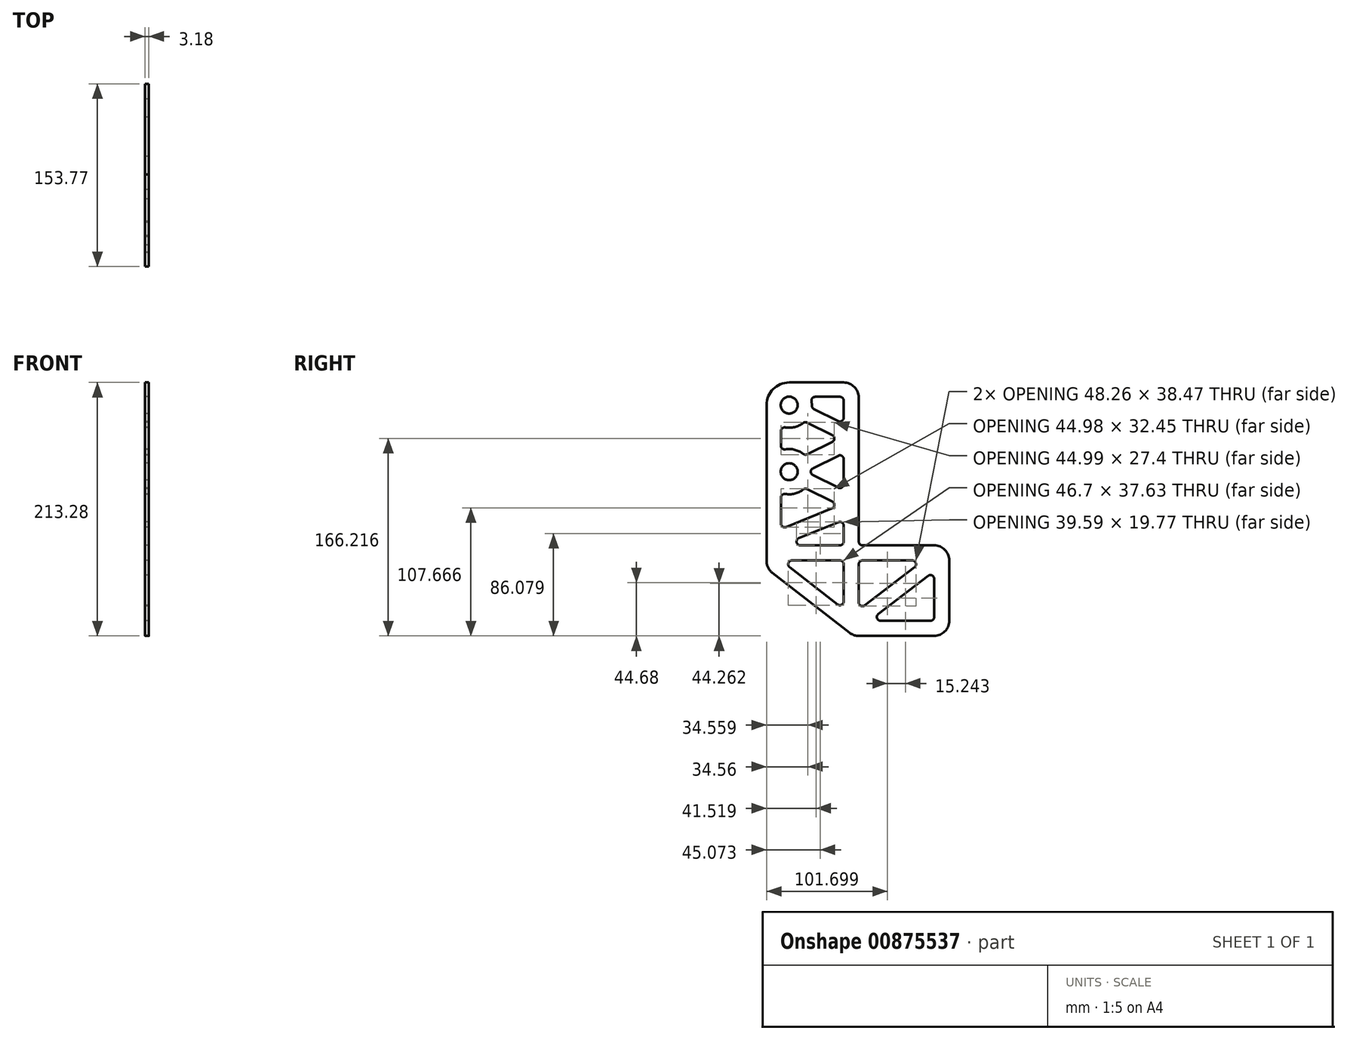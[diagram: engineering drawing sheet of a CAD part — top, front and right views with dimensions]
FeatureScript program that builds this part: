
annotation { "Feature Type Name" : "Feature", "Feature Type Description" : "" }
export const myFeature = defineFeature(function(context is Context, id is Id, definition is map)
    precondition{}
    {
        {
            var Q0;
            Q0=qCreatedBy(makeId("Right.planeOp"),FACE);
            var sketch = newSketch(context, id + "F0", { "sketchPlane" : qUnion([Q0])});
            skLineSegment(sketch, "E0.bottom", {"start": v(25.4, -41.28) * mm, "end": v(-34.93, -41.28) * mm});
            skLineSegment(sketch, "E0.top", {"start": v(38.1, 41.28) * mm, "end": v(-38.1, 41.27) * mm, "construction": true});
            skLineSegment(sketch, "E0.left", {"start": v(38.1, -41.27) * mm, "end": v(38.1, 41.28) * mm, "construction": true});
            skLineSegment(sketch, "E0.right", {"start": v(-38.1, -38.1) * mm, "end": v(-38.1, 41.27) * mm});
            skPoint(sketch, "E0.middle", {"position": v(0, 0) * mm});
            skCircle(sketch, "E1", {"center": v(0, 28.58) * mm, "radius": 6.35 * mm, "construction": true});
            skLineSegment(sketch, "E2", {"start": v(0, 28.57) * mm, "end": v(-38.1, 47.58) * mm, "construction": true});
            skLineSegment(sketch, "E3", {"start": v(0, 28.57) * mm, "end": v(-38.1, 25.48) * mm, "construction": true});
            skLineSegment(sketch, "E4", {"start": v(0, 28.58) * mm, "end": v(-38.1, 28.57) * mm, "construction": true});
            skLineSegment(sketch, "E5", {"start": v(38.1, -53.98) * mm, "end": v(38.1, -104.78) * mm});
            skLineSegment(sketch, "E6", {"start": v(-38.1, 47.58) * mm, "end": v(-795.56, 425.31) * mm, "construction": true});
            skLineSegment(sketch, "E7", {"start": v(-795.56, 425.31) * mm, "end": v(-1159.25, 606.68) * mm, "construction": true});
            skLineSegment(sketch, "E8", {"start": v(-1159.25, 606.68) * mm, "end": v(-1295.27, 333.92) * mm, "construction": true});
            skLineSegment(sketch, "E9", {"start": v(38.1, -117.48) * mm, "end": v(38.1, -1990.73) * mm, "construction": true});
            skLineSegment(sketch, "E10", {"start": v(-1295.27, 333.92) * mm, "end": v(-1295.27, -1990.73) * mm, "construction": true});
            skLineSegment(sketch, "E11", {"start": v(-1295.27, -1990.73) * mm, "end": v(38.1, -1990.73) * mm, "construction": true});
            skLineSegment(sketch, "E12", {"start": v(-860.82, -41.27) * mm, "end": v(-1265.64, -77.12) * mm, "construction": true});
            skLineSegment(sketch, "E13", {"start": v(-1265.64, -77.12) * mm, "end": v(-1238.76, -380.73) * mm, "construction": true});
            skLineSegment(sketch, "E14", {"start": v(-1238.76, -380.73) * mm, "end": v(-1238.76, -1990.73) * mm, "construction": true});
            skCircle(sketch, "E15", {"center": v(-96.62, 76.76) * mm, "radius": 6.99 * mm});
            skCircle(sketch, "E16", {"center": v(-96.62, 20.74) * mm, "radius": 6.99 * mm});
            skLineSegment(sketch, "E17", {"start": v(-860.82, -41.28) * mm, "end": v(-89.66, 21.3) * mm, "construction": true});
            skLineSegment(sketch, "E18", {"start": v(-38.1, 47.58) * mm, "end": v(-38.1, 83.1) * mm});
            skLineSegment(sketch, "E19", {"start": v(-38.1, 47.58) * mm, "end": v(-38.1, 41.28) * mm});
            skArc(sketch, "E20", {"start": v(-99.88, 57.99) * mm, "mid": v(-91.97, 58.28) * mm, "end": v(-84.86, 61.77) * mm});
            skLineSegment(sketch, "E21", {"start": v(-115.67, 76.76) * mm, "end": v(-115.67, 19.19) * mm});
            skLineSegment(sketch, "E22", {"start": v(-115.67, 19.19) * mm, "end": v(-115.67, -54.47) * mm});
            skLineSegment(sketch, "E23", {"start": v(-110.75, -64.5) * mm, "end": v(-45.88, -114.81) * mm});
            skLineSegment(sketch, "E24", {"start": v(-103.6, -1.16) * mm, "end": v(-103.6, -22.87) * mm});
            skLineSegment(sketch, "E25", {"start": v(25.4, -117.48) * mm, "end": v(-38.1, -117.48) * mm});
            skLineSegment(sketch, "E26", {"start": v(-81.48, 35.38) * mm, "end": v(-60.37, 45.9) * mm});
            skLineSegment(sketch, "E27", {"start": v(-81.48, 62.11) * mm, "end": v(-60.37, 51.59) * mm});
            skLineSegment(sketch, "E28", {"start": v(-75.81, 73.48) * mm, "end": v(-55.4, 63.3) * mm});
            skLineSegment(sketch, "E29", {"start": v(-103.6, 76.76) * mm, "end": v(-103.6, 76.76) * mm});
            skLineSegment(sketch, "E30", {"start": v(-96.62, 95.8) * mm, "end": v(-50.8, 95.8) * mm});
            skLineSegment(sketch, "E31", {"start": v(-74.72, 83.74) * mm, "end": v(-53.98, 83.74) * mm});
            skPoint(sketch, "E32", {"position": v(-83.38, 34.43) * mm});
            skPoint(sketch, "E33", {"position": v(-50.8, 46.81) * mm});
            skPoint(sketch, "E34", {"position": v(-83.38, 63.06) * mm});
            skPoint(sketch, "E35", {"position": v(-77.71, 74.42) * mm});
            skPoint(sketch, "E36", {"position": v(-50.8, 83.74) * mm});
            skPoint(sketch, "E37", {"position": v(-83.38, 7.04) * mm});
            skLineSegment(sketch, "E38", {"start": v(-55.92, -90.95) * mm, "end": v(-96.27, -59.66) * mm});
            skLineSegment(sketch, "E39", {"start": v(-94.33, -53.98) * mm, "end": v(-53.97, -53.98) * mm});
            skLineSegment(sketch, "E40", {"start": v(-60.6, -10.22) * mm, "end": v(-99.24, -25.82) * mm});
            skLineSegment(sketch, "E41", {"start": v(-55.16, -21.72) * mm, "end": v(-88.45, -35.16) * mm});
            skLineSegment(sketch, "E42", {"start": v(-87.26, -41.28) * mm, "end": v(-53.97, -41.28) * mm});
            skLineSegment(sketch, "E43", {"start": v(-34.92, -53.98) * mm, "end": v(6.98, -53.98) * mm});
            skLineSegment(sketch, "E44", {"start": v(8.91, -59.67) * mm, "end": v(-33, -91.8) * mm});
            skLineSegment(sketch, "E45", {"start": v(-19.68, -104.78) * mm, "end": v(22.23, -104.78) * mm});
            skLineSegment(sketch, "E46", {"start": v(25.4, -101.6) * mm, "end": v(25.4, -69.47) * mm});
            skLineSegment(sketch, "E47", {"start": v(20.3, -66.95) * mm, "end": v(-21.61, -99.08) * mm});
            skArc(sketch, "E48.trimOffspring", {"start": v(-99.88, 1.97) * mm, "mid": v(-91.97, 2.26) * mm, "end": v(-84.86, 5.75) * mm});
            skLineSegment(sketch, "E49.trimOffspring", {"start": v(-50.8, 24.45) * mm, "end": v(-38.1, 25.48) * mm, "construction": true});
            skLineSegment(sketch, "E50.trimOffspring", {"start": v(-103.6, 54.86) * mm, "end": v(-103.6, 42.63) * mm});
            skArc(sketch, "E51.trimOffspring", {"start": v(-96.62, 95.8) * mm, "mid": v(-110.09, 90.23) * mm, "end": v(-115.67, 76.76) * mm});
            skLineSegment(sketch, "E52.trimOffspring", {"start": v(-50.8, 80.57) * mm, "end": v(-50.8, 66.14) * mm});
            skArc(sketch, "E53.trimOffspring", {"start": v(-84.86, 35.72) * mm, "mid": v(-91.97, 39.2) * mm, "end": v(-99.88, 39.5) * mm});
            skLineSegment(sketch, "E54.trimOffspring", {"start": v(-50.8, -57.15) * mm, "end": v(-50.8, -88.45) * mm});
            skLineSegment(sketch, "E55", {"start": v(-50.8, -24.66) * mm, "end": v(-50.8, -38.1) * mm});
            skArc(sketch, "E56.filletArc", {"start": v(-38.1, 83.1) * mm, "mid": v(-41.82, 92.09) * mm, "end": v(-50.8, 95.8) * mm});
            skPoint(sketch, "E57.visualSharp", {"position": v(38.1, -41.28) * mm});
            skArc(sketch, "E57.filletArc", {"start": v(38.1, -53.98) * mm, "mid": v(34.38, -45) * mm, "end": v(25.4, -41.28) * mm});
            skPoint(sketch, "E58.visualSharp", {"position": v(38.1, -117.48) * mm});
            skArc(sketch, "E58.filletArc", {"start": v(25.4, -117.48) * mm, "mid": v(34.38, -113.76) * mm, "end": v(38.1, -104.78) * mm});
            skPoint(sketch, "E59.visualSharp", {"position": v(-115.67, -60.69) * mm});
            skArc(sketch, "E59.filletArc", {"start": v(-115.67, -54.47) * mm, "mid": v(-114.37, -60.06) * mm, "end": v(-110.75, -64.5) * mm});
            skPoint(sketch, "E60.newPointA", {"position": v(-42.45, -117.48) * mm});
            skArc(sketch, "E60.filletArc", {"start": v(-45.88, -114.81) * mm, "mid": v(-42.21, -116.8) * mm, "end": v(-38.1, -117.48) * mm});
            skPoint(sketch, "E61.visualSharp", {"position": v(-50.8, -41.28) * mm});
            skArc(sketch, "E61.filletArc", {"start": v(-53.97, -41.28) * mm, "mid": v(-51.73, -40.35) * mm, "end": v(-50.8, -38.1) * mm});
            skPoint(sketch, "E62.visualSharp", {"position": v(-50.8, -19.96) * mm});
            skArc(sketch, "E62.filletArc", {"start": v(-50.8, -24.66) * mm, "mid": v(-52.2, -22.03) * mm, "end": v(-55.16, -21.72) * mm});
            skPoint(sketch, "E63.visualSharp", {"position": v(-103.6, -41.28) * mm});
            skArc(sketch, "E63.filletArc", {"start": v(-88.45, -35.16) * mm, "mid": v(-90.37, -38.7) * mm, "end": v(-87.26, -41.28) * mm});
            skPoint(sketch, "E64.visualSharp", {"position": v(-103.6, -53.98) * mm});
            skArc(sketch, "E64.filletArc", {"start": v(-94.33, -53.98) * mm, "mid": v(-97.33, -56.12) * mm, "end": v(-96.27, -59.66) * mm});
            skPoint(sketch, "E65.visualSharp", {"position": v(-50.8, -53.98) * mm});
            skArc(sketch, "E65.filletArc", {"start": v(-50.8, -57.15) * mm, "mid": v(-51.73, -54.9) * mm, "end": v(-53.97, -53.98) * mm});
            skPoint(sketch, "E66.visualSharp", {"position": v(-50.8, -94.93) * mm});
            skArc(sketch, "E66.filletArc", {"start": v(-55.92, -90.95) * mm, "mid": v(-52.58, -91.3) * mm, "end": v(-50.8, -88.45) * mm});
            skPoint(sketch, "E67.visualSharp", {"position": v(-38.1, -95.72) * mm});
            skArc(sketch, "E67.filletArc", {"start": v(-38.1, -89.28) * mm, "mid": v(-36.33, -92.13) * mm, "end": v(-33, -91.8) * mm});
            skPoint(sketch, "E68.visualSharp", {"position": v(-38.1, -53.98) * mm});
            skArc(sketch, "E68.filletArc", {"start": v(-34.92, -53.98) * mm, "mid": v(-37.17, -54.9) * mm, "end": v(-38.1, -57.15) * mm});
            skPoint(sketch, "E69.visualSharp", {"position": v(16.34, -53.98) * mm});
            skArc(sketch, "E69.filletArc", {"start": v(8.91, -59.67) * mm, "mid": v(9.99, -56.13) * mm, "end": v(6.98, -53.98) * mm});
            skPoint(sketch, "E70.visualSharp", {"position": v(25.4, -63.03) * mm});
            skArc(sketch, "E70.filletArc", {"start": v(25.4, -69.47) * mm, "mid": v(23.63, -66.62) * mm, "end": v(20.3, -66.95) * mm});
            skPoint(sketch, "E71.visualSharp", {"position": v(-29.04, -104.78) * mm});
            skArc(sketch, "E71.filletArc", {"start": v(-21.61, -99.08) * mm, "mid": v(-22.69, -102.62) * mm, "end": v(-19.68, -104.78) * mm});
            skArc(sketch, "E72.filletArc", {"start": v(22.23, -104.78) * mm, "mid": v(24.47, -103.85) * mm, "end": v(25.4, -101.6) * mm});
            skPoint(sketch, "E73.visualSharp", {"position": v(-103.6, -27.58) * mm});
            skArc(sketch, "E73.filletArc", {"start": v(-103.6, -22.87) * mm, "mid": v(-102.2, -25.5) * mm, "end": v(-99.24, -25.82) * mm});
            skPoint(sketch, "E74.visualSharp", {"position": v(-50.8, -6.26) * mm});
            skArc(sketch, "E74.filletArc", {"start": v(-60.6, -10.22) * mm, "mid": v(-58.62, -7.4) * mm, "end": v(-60.37, -4.43) * mm});
            skPoint(sketch, "E75.visualSharp", {"position": v(-103.6, 3.01) * mm});
            skArc(sketch, "E75.filletArc", {"start": v(-99.88, 1.97) * mm, "mid": v(-102.47, 1.27) * mm, "end": v(-103.6, -1.16) * mm});
            skPoint(sketch, "E76.visualSharp", {"position": v(-38.1, -41.28) * mm});
            skArc(sketch, "E76.filletArc", {"start": v(-38.1, -38.1) * mm, "mid": v(-37.17, -40.35) * mm, "end": v(-34.93, -41.28) * mm});
            skArc(sketch, "E77.filletArc", {"start": v(-84.86, 35.72) * mm, "mid": v(-83.22, 35.06) * mm, "end": v(-81.48, 35.38) * mm});
            skPoint(sketch, "E78.visualSharp", {"position": v(-103.6, 38.46) * mm});
            skArc(sketch, "E78.filletArc", {"start": v(-103.6, 42.63) * mm, "mid": v(-102.47, 40.2) * mm, "end": v(-99.88, 39.5) * mm});
            skPoint(sketch, "E79.visualSharp", {"position": v(-103.6, 59.03) * mm});
            skArc(sketch, "E79.filletArc", {"start": v(-99.88, 57.99) * mm, "mid": v(-102.47, 57.3) * mm, "end": v(-103.6, 54.86) * mm});
            skArc(sketch, "E80.filletArc", {"start": v(-60.37, 45.9) * mm, "mid": v(-58.62, 48.75) * mm, "end": v(-60.37, 51.59) * mm});
            skPoint(sketch, "E81.visualSharp", {"position": v(-78.9, 83.74) * mm});
            skArc(sketch, "E81.filletArc", {"start": v(-74.72, 83.74) * mm, "mid": v(-77.15, 82.61) * mm, "end": v(-77.85, 80.02) * mm});
            skArc(sketch, "E82.filletArc", {"start": v(-50.8, 80.57) * mm, "mid": v(-51.73, 82.81) * mm, "end": v(-53.98, 83.74) * mm});
            skPoint(sketch, "E83.visualSharp", {"position": v(-50.8, 4.98) * mm});
            skLineSegment(sketch, "E84", {"start": v(-50.8, 80.57) * mm, "end": v(-50.8, 61) * mm, "construction": true});
            skArc(sketch, "E85.filletArc", {"start": v(-55.4, 63.3) * mm, "mid": v(-52.3, 63.44) * mm, "end": v(-50.8, 66.14) * mm});
            skLineSegment(sketch, "E86", {"start": v(-38.1, -57.15) * mm, "end": v(-38.1, -89.28) * mm});
            skLineSegment(sketch, "E87", {"start": v(-50.8, 24.45) * mm, "end": v(-96.62, 20.74) * mm, "construction": true});
            skCircle(sketch, "E88", {"center": v(-96.62, 20.74) * mm, "radius": 19.05 * mm, "construction": true});
            skLineSegment(sketch, "E89", {"start": v(-50.8, 61) * mm, "end": v(-55.4, 63.3) * mm, "construction": true});
            skLineSegment(sketch, "E90", {"start": v(-77.71, 74.42) * mm, "end": v(-93.28, 82.9) * mm, "construction": true});
            skLineSegment(sketch, "E91", {"start": v(-50.8, 10.11) * mm, "end": v(-50.8, 31.36) * mm});
            skLineSegment(sketch, "E92", {"start": v(-50.8, 4.98) * mm, "end": v(-50.8, -94.93) * mm, "construction": true});
            skLineSegment(sketch, "E93", {"start": v(-103.6, -22.87) * mm, "end": v(-103.6, -53.98) * mm, "construction": true});
            skArc(sketch, "E94.filletArc", {"start": v(-50.8, 31.36) * mm, "mid": v(-52.3, 34.06) * mm, "end": v(-55.4, 34.2) * mm});
            skLineSegment(sketch, "E95", {"start": v(-50.8, 31.36) * mm, "end": v(-50.8, 46.81) * mm, "construction": true});
            skArc(sketch, "E96.filletArc", {"start": v(-55.4, 7.27) * mm, "mid": v(-52.3, 7.41) * mm, "end": v(-50.8, 10.11) * mm});
            skLineSegment(sketch, "E97", {"start": v(-50.8, 4.98) * mm, "end": v(-50.8, 10.11) * mm, "construction": true});
            skLineSegment(sketch, "E98", {"start": v(-60.6, -10.22) * mm, "end": v(-50.8, -6.26) * mm, "construction": true});
            skLineSegment(sketch, "E99", {"start": v(-53.97, -41.28) * mm, "end": v(-50.8, -41.28) * mm, "construction": true});
            skLineSegment(sketch, "E100", {"start": v(-55.16, -21.72) * mm, "end": v(-50.8, -19.96) * mm, "construction": true});
            skLineSegment(sketch, "E101", {"start": v(-50.8, -94.93) * mm, "end": v(-55.92, -90.95) * mm, "construction": true});
            skLineSegment(sketch, "E102", {"start": v(-67.24, 42.48) * mm, "end": v(-61.57, 31.12) * mm, "construction": true});
            skPoint(sketch, "E103", {"position": v(-64.4, 36.8) * mm});
            skLineSegment(sketch, "E104", {"start": v(-96.62, 20.74) * mm, "end": v(-64.4, 36.8) * mm, "construction": true});
            skLineSegment(sketch, "E105", {"start": v(-67.24, 42.48) * mm, "end": v(-81.48, 35.38) * mm});
            skLineSegment(sketch, "E106", {"start": v(-50.8, 36.49) * mm, "end": v(-55.4, 34.2) * mm, "construction": true});
            skLineSegment(sketch, "E107", {"start": v(-55.4, 34.2) * mm, "end": v(-61.57, 31.12) * mm});
            skLineSegment(sketch, "E108", {"start": v(-67.24, 42.48) * mm, "end": v(-96.85, 27.72) * mm});
            skLineSegment(sketch, "E109", {"start": v(-60.37, -4.43) * mm, "end": v(-81.48, 6.1) * mm});
            skLineSegment(sketch, "E110", {"start": v(-83.38, 7.04) * mm, "end": v(-96.85, 13.75) * mm});
            skLineSegment(sketch, "E111", {"start": v(-50.8, 4.98) * mm, "end": v(-55.4, 7.27) * mm, "construction": true});
            skLineSegment(sketch, "E112", {"start": v(-61.47, 10.3) * mm, "end": v(-67.14, -1.06) * mm, "construction": true});
            skLineSegment(sketch, "E113", {"start": v(-64.3, 4.62) * mm, "end": v(-96.62, 20.74) * mm, "construction": true});
            skArc(sketch, "E114.filletArc", {"start": v(-81.48, 6.1) * mm, "mid": v(-83.22, 6.4) * mm, "end": v(-84.86, 5.75) * mm});
            skLineSegment(sketch, "E115", {"start": v(-81.48, 6.1) * mm, "end": v(-83.38, 7.04) * mm});
            skLineSegment(sketch, "E116", {"start": v(25.4, -63.03) * mm, "end": v(25.4, -53.98) * mm, "construction": true});
            skLineSegment(sketch, "E117", {"start": v(16.34, -53.98) * mm, "end": v(25.4, -53.97) * mm, "construction": true});
            skLineSegment(sketch, "E118", {"start": v(-38.1, -95.72) * mm, "end": v(-38.1, -104.78) * mm, "construction": true});
            skLineSegment(sketch, "E119", {"start": v(-29.04, -104.78) * mm, "end": v(-38.1, -104.78) * mm, "construction": true});
            skLineSegment(sketch, "E120", {"start": v(-38.1, -57.15) * mm, "end": v(-38.1, -53.98) * mm, "construction": true});
            skLineSegment(sketch, "E121", {"start": v(-34.92, -53.98) * mm, "end": v(-38.1, -53.98) * mm, "construction": true});
            skLineSegment(sketch, "E122", {"start": v(-45.88, -114.81) * mm, "end": v(-42.45, -117.48) * mm, "construction": true});
            skLineSegment(sketch, "E123", {"start": v(-38.1, -117.48) * mm, "end": v(-42.45, -117.48) * mm, "construction": true});
            skArc(sketch, "E124.trimOffspring", {"start": v(-77.57, 76.38) * mm, "mid": v(-77.62, 78.2) * mm, "end": v(-77.85, 80.02) * mm});
            skLineSegment(sketch, "E125", {"start": v(-76.7, 23.58) * mm, "end": v(-55.4, 34.2) * mm});
            skLineSegment(sketch, "E126", {"start": v(-55.4, 7.27) * mm, "end": v(-76.7, 17.9) * mm});
            skLineSegment(sketch, "E127", {"start": v(-76.7, 23.58) * mm, "end": v(-91.18, 16.35) * mm, "construction": true});
            skLineSegment(sketch, "E128", {"start": v(-76.7, 17.9) * mm, "end": v(-91.18, 25.12) * mm, "construction": true});
            skArc(sketch, "E129.filletArc", {"start": v(-76.7, 23.58) * mm, "mid": v(-78.45, 20.74) * mm, "end": v(-76.7, 17.9) * mm});
            skArc(sketch, "E130.filletArc", {"start": v(-81.48, 62.11) * mm, "mid": v(-83.22, 62.43) * mm, "end": v(-84.86, 61.77) * mm});
            skArc(sketch, "E131.filletArc", {"start": v(-77.57, 76.38) * mm, "mid": v(-77.11, 74.68) * mm, "end": v(-75.81, 73.48) * mm});
            skCircle(sketch, "E132", {"center": v(-96.62, 76.76) * mm, "radius": 19.05 * mm, "construction": true});
            skLineSegment(sketch, "E133", {"start": v(-61.58, 52.19) * mm, "end": v(-55.91, 63.55) * mm, "construction": true});
            skPoint(sketch, "E134", {"position": v(-58.74, 57.87) * mm});
            skSolve(sketch);
        }
        {
            var Q0;
            Q0=makeQuery(id+"F0.imprint","IMPRINT",FACE,{"disambiguationData":[TD([[makeQuery(id+"F0.imprint","IMPRINT",EDGE,{"derivedFrom":sQuery(id+"F0.wireOp",EDGE,"E0.bottom")}),1.0]])]});
            var Q1;
            {var subQ0=sQuery(id+"F0.wireOp",EDGE,"E16");var subQ1=makeQuery(id+"F0.imprint","IMPRINT",VERTEX,{"disambiguationData":[OD(0.0)],"derivedFrom":subQ0});Q1=makeQuery(id+"F0.imprint","IMPRINT",FACE,{"disambiguationData":[TD([[makeQuery(id+"F0.imprint","IMPRINT",EDGE,{"disambiguationData":[TD([[subQ1,-1.0]])],"derivedFrom":subQ0}),1.0]])]});}
            var Q2;
            Q2=makeQuery(id+"F0.imprint","IMPRINT",FACE,{"disambiguationData":[TD([[makeQuery(id+"F0.imprint","IMPRINT",EDGE,{"derivedFrom":sQuery(id+"F0.wireOp",EDGE,"E15")}),1.0]])]});
            extrude(context, id + "F1", {"entities" : qUnion([Q0, Q1, Q2]), "depth" : 3.17 * mm, "offsetDistance" : 25.4 * mm});
        }
        {
            var Q0;
            Q0=makeQuery(id+"F1.opExtrude","CAP_FACE",FACE,{"disambiguationData":[OSD([sQuery(id+"F0.wireOp",EDGE,"E0.bottom"),sQuery(id+"F0.wireOp",EDGE,"E0.right"),sQuery(id+"F0.wireOp",EDGE,"E5"),sQuery(id+"F0.wireOp",EDGE,"E18"),sQuery(id+"F0.wireOp",EDGE,"E19"),sQuery(id+"F0.wireOp",EDGE,"E20"),sQuery(id+"F0.wireOp",EDGE,"E21"),sQuery(id+"F0.wireOp",EDGE,"E22"),sQuery(id+"F0.wireOp",EDGE,"E23"),sQuery(id+"F0.wireOp",EDGE,"E24"),sQuery(id+"F0.wireOp",EDGE,"E25"),sQuery(id+"F0.wireOp",EDGE,"E26"),sQuery(id+"F0.wireOp",EDGE,"E27"),sQuery(id+"F0.wireOp",EDGE,"E28"),sQuery(id+"F0.wireOp",EDGE,"E30"),sQuery(id+"F0.wireOp",EDGE,"E31"),sQuery(id+"F0.wireOp",EDGE,"E38"),sQuery(id+"F0.wireOp",EDGE,"E39"),sQuery(id+"F0.wireOp",EDGE,"E40"),sQuery(id+"F0.wireOp",EDGE,"E41"),sQuery(id+"F0.wireOp",EDGE,"E42"),sQuery(id+"F0.wireOp",EDGE,"E43"),sQuery(id+"F0.wireOp",EDGE,"E44"),sQuery(id+"F0.wireOp",EDGE,"E45"),sQuery(id+"F0.wireOp",EDGE,"E46"),sQuery(id+"F0.wireOp",EDGE,"E47"),sQuery(id+"F0.wireOp",EDGE,"E48.trimOffspring"),sQuery(id+"F0.wireOp",EDGE,"E50.trimOffspring"),sQuery(id+"F0.wireOp",EDGE,"E51.trimOffspring"),sQuery(id+"F0.wireOp",EDGE,"E52.trimOffspring"),sQuery(id+"F0.wireOp",EDGE,"E53.trimOffspring"),sQuery(id+"F0.wireOp",EDGE,"E54.trimOffspring"),sQuery(id+"F0.wireOp",EDGE,"E55"),sQuery(id+"F0.wireOp",EDGE,"E56.filletArc"),sQuery(id+"F0.wireOp",EDGE,"E57.filletArc"),sQuery(id+"F0.wireOp",EDGE,"E58.filletArc"),sQuery(id+"F0.wireOp",EDGE,"E59.filletArc"),sQuery(id+"F0.wireOp",EDGE,"E60.filletArc"),sQuery(id+"F0.wireOp",EDGE,"E61.filletArc"),sQuery(id+"F0.wireOp",EDGE,"E62.filletArc"),sQuery(id+"F0.wireOp",EDGE,"E63.filletArc"),sQuery(id+"F0.wireOp",EDGE,"E64.filletArc"),sQuery(id+"F0.wireOp",EDGE,"E65.filletArc"),sQuery(id+"F0.wireOp",EDGE,"E66.filletArc"),sQuery(id+"F0.wireOp",EDGE,"E67.filletArc"),sQuery(id+"F0.wireOp",EDGE,"E68.filletArc"),sQuery(id+"F0.wireOp",EDGE,"E69.filletArc"),sQuery(id+"F0.wireOp",EDGE,"E70.filletArc"),sQuery(id+"F0.wireOp",EDGE,"E71.filletArc"),sQuery(id+"F0.wireOp",EDGE,"E72.filletArc"),sQuery(id+"F0.wireOp",EDGE,"E73.filletArc"),sQuery(id+"F0.wireOp",EDGE,"E74.filletArc"),sQuery(id+"F0.wireOp",EDGE,"E75.filletArc"),sQuery(id+"F0.wireOp",EDGE,"E76.filletArc"),sQuery(id+"F0.wireOp",EDGE,"E77.filletArc"),sQuery(id+"F0.wireOp",EDGE,"E78.filletArc"),sQuery(id+"F0.wireOp",EDGE,"E79.filletArc"),sQuery(id+"F0.wireOp",EDGE,"E80.filletArc"),sQuery(id+"F0.wireOp",EDGE,"E81.filletArc"),sQuery(id+"F0.wireOp",EDGE,"E82.filletArc"),sQuery(id+"F0.wireOp",EDGE,"E85.filletArc"),sQuery(id+"F0.wireOp",EDGE,"E86"),sQuery(id+"F0.wireOp",EDGE,"E91"),sQuery(id+"F0.wireOp",EDGE,"E94.filletArc"),sQuery(id+"F0.wireOp",EDGE,"E96.filletArc"),sQuery(id+"F0.wireOp",EDGE,"E108"),sQuery(id+"F0.wireOp",EDGE,"E109"),sQuery(id+"F0.wireOp",EDGE,"E114.filletArc"),sQuery(id+"F0.wireOp",EDGE,"E124.trimOffspring"),sQuery(id+"F0.wireOp",EDGE,"E125"),sQuery(id+"F0.wireOp",EDGE,"E126"),sQuery(id+"F0.wireOp",EDGE,"E129.filletArc"),sQuery(id+"F0.wireOp",EDGE,"E130.filletArc"),sQuery(id+"F0.wireOp",EDGE,"E131.filletArc")])],"isStart":true});
            var sketch = newSketch(context, id + "F2", { "sketchPlane" : qUnion([Q0])});
            skPoint(sketch, "E135", {"position": v(96.62, 20.74) * mm});
            skPoint(sketch, "E136", {"position": v(96.62, 76.76) * mm});
            skSolve(sketch);
        }
        {
            var Q0;
            Q0=sQuery(id+"F2.wireOp",VERTEX,"E135");
            var Q1;
            Q1=sQuery(id+"F2.wireOp",VERTEX,"E136");
            var Q2;
            Q2=makeQuery(id+"F1.opExtrude","SWEPT_BODY",BODY,{"disambiguationData":[OSD([sQuery(id+"F0.wireOp",EDGE,"E0.bottom"),sQuery(id+"F0.wireOp",EDGE,"E0.right"),sQuery(id+"F0.wireOp",EDGE,"E5"),sQuery(id+"F0.wireOp",EDGE,"E18"),sQuery(id+"F0.wireOp",EDGE,"E19"),sQuery(id+"F0.wireOp",EDGE,"E20"),sQuery(id+"F0.wireOp",EDGE,"E21"),sQuery(id+"F0.wireOp",EDGE,"E22"),sQuery(id+"F0.wireOp",EDGE,"E23"),sQuery(id+"F0.wireOp",EDGE,"E24"),sQuery(id+"F0.wireOp",EDGE,"E25"),sQuery(id+"F0.wireOp",EDGE,"E26"),sQuery(id+"F0.wireOp",EDGE,"E27"),sQuery(id+"F0.wireOp",EDGE,"E28"),sQuery(id+"F0.wireOp",EDGE,"E30"),sQuery(id+"F0.wireOp",EDGE,"E31"),sQuery(id+"F0.wireOp",EDGE,"E38"),sQuery(id+"F0.wireOp",EDGE,"E39"),sQuery(id+"F0.wireOp",EDGE,"E40"),sQuery(id+"F0.wireOp",EDGE,"E41"),sQuery(id+"F0.wireOp",EDGE,"E42"),sQuery(id+"F0.wireOp",EDGE,"E43"),sQuery(id+"F0.wireOp",EDGE,"E44"),sQuery(id+"F0.wireOp",EDGE,"E45"),sQuery(id+"F0.wireOp",EDGE,"E46"),sQuery(id+"F0.wireOp",EDGE,"E47"),sQuery(id+"F0.wireOp",EDGE,"E48.trimOffspring"),sQuery(id+"F0.wireOp",EDGE,"E50.trimOffspring"),sQuery(id+"F0.wireOp",EDGE,"E51.trimOffspring"),sQuery(id+"F0.wireOp",EDGE,"E52.trimOffspring"),sQuery(id+"F0.wireOp",EDGE,"E53.trimOffspring"),sQuery(id+"F0.wireOp",EDGE,"E54.trimOffspring"),sQuery(id+"F0.wireOp",EDGE,"E55"),sQuery(id+"F0.wireOp",EDGE,"E56.filletArc"),sQuery(id+"F0.wireOp",EDGE,"E57.filletArc"),sQuery(id+"F0.wireOp",EDGE,"E58.filletArc"),sQuery(id+"F0.wireOp",EDGE,"E59.filletArc"),sQuery(id+"F0.wireOp",EDGE,"E60.filletArc"),sQuery(id+"F0.wireOp",EDGE,"E61.filletArc"),sQuery(id+"F0.wireOp",EDGE,"E62.filletArc"),sQuery(id+"F0.wireOp",EDGE,"E63.filletArc"),sQuery(id+"F0.wireOp",EDGE,"E64.filletArc"),sQuery(id+"F0.wireOp",EDGE,"E65.filletArc"),sQuery(id+"F0.wireOp",EDGE,"E66.filletArc"),sQuery(id+"F0.wireOp",EDGE,"E67.filletArc"),sQuery(id+"F0.wireOp",EDGE,"E68.filletArc"),sQuery(id+"F0.wireOp",EDGE,"E69.filletArc"),sQuery(id+"F0.wireOp",EDGE,"E70.filletArc"),sQuery(id+"F0.wireOp",EDGE,"E71.filletArc"),sQuery(id+"F0.wireOp",EDGE,"E72.filletArc"),sQuery(id+"F0.wireOp",EDGE,"E73.filletArc"),sQuery(id+"F0.wireOp",EDGE,"E74.filletArc"),sQuery(id+"F0.wireOp",EDGE,"E75.filletArc"),sQuery(id+"F0.wireOp",EDGE,"E76.filletArc"),sQuery(id+"F0.wireOp",EDGE,"E77.filletArc"),sQuery(id+"F0.wireOp",EDGE,"E78.filletArc"),sQuery(id+"F0.wireOp",EDGE,"E79.filletArc"),sQuery(id+"F0.wireOp",EDGE,"E80.filletArc"),sQuery(id+"F0.wireOp",EDGE,"E81.filletArc"),sQuery(id+"F0.wireOp",EDGE,"E82.filletArc"),sQuery(id+"F0.wireOp",EDGE,"E85.filletArc"),sQuery(id+"F0.wireOp",EDGE,"E86"),sQuery(id+"F0.wireOp",EDGE,"E91"),sQuery(id+"F0.wireOp",EDGE,"E94.filletArc"),sQuery(id+"F0.wireOp",EDGE,"E96.filletArc"),sQuery(id+"F0.wireOp",EDGE,"E108"),sQuery(id+"F0.wireOp",EDGE,"E109"),sQuery(id+"F0.wireOp",EDGE,"E114.filletArc"),sQuery(id+"F0.wireOp",EDGE,"E124.trimOffspring"),sQuery(id+"F0.wireOp",EDGE,"E125"),sQuery(id+"F0.wireOp",EDGE,"E126"),sQuery(id+"F0.wireOp",EDGE,"E129.filletArc"),sQuery(id+"F0.wireOp",EDGE,"E130.filletArc"),sQuery(id+"F0.wireOp",EDGE,"E131.filletArc")])]});
            hole(context, id + "F3", {"style" : HoleStyle.SIMPLE, "endStyle" : HoleEndStyle.THROUGH, "standardTappedOrClearance" : lookupTablePath({ "fit" : "Normal (ASME)", "standard" : "ANSI", "size" : "1/2", "type" : "Clearance" }), "standardBlindInLast" : lookupTablePath({ "fit" : "Normal", "standard" : "ANSI", "size" : "1/2", "type" : "Clearance" }), "holeDiameter" : 14.27 * mm, "majorDiameter" : 12.7 * mm, "isTappedThrough" : true, "tappedDepth" : 12.7 * mm, "tapClearance" : 3, "locations" : qUnion([Q0, Q1]), "scope" : qUnion([Q2])});
        }
    });
